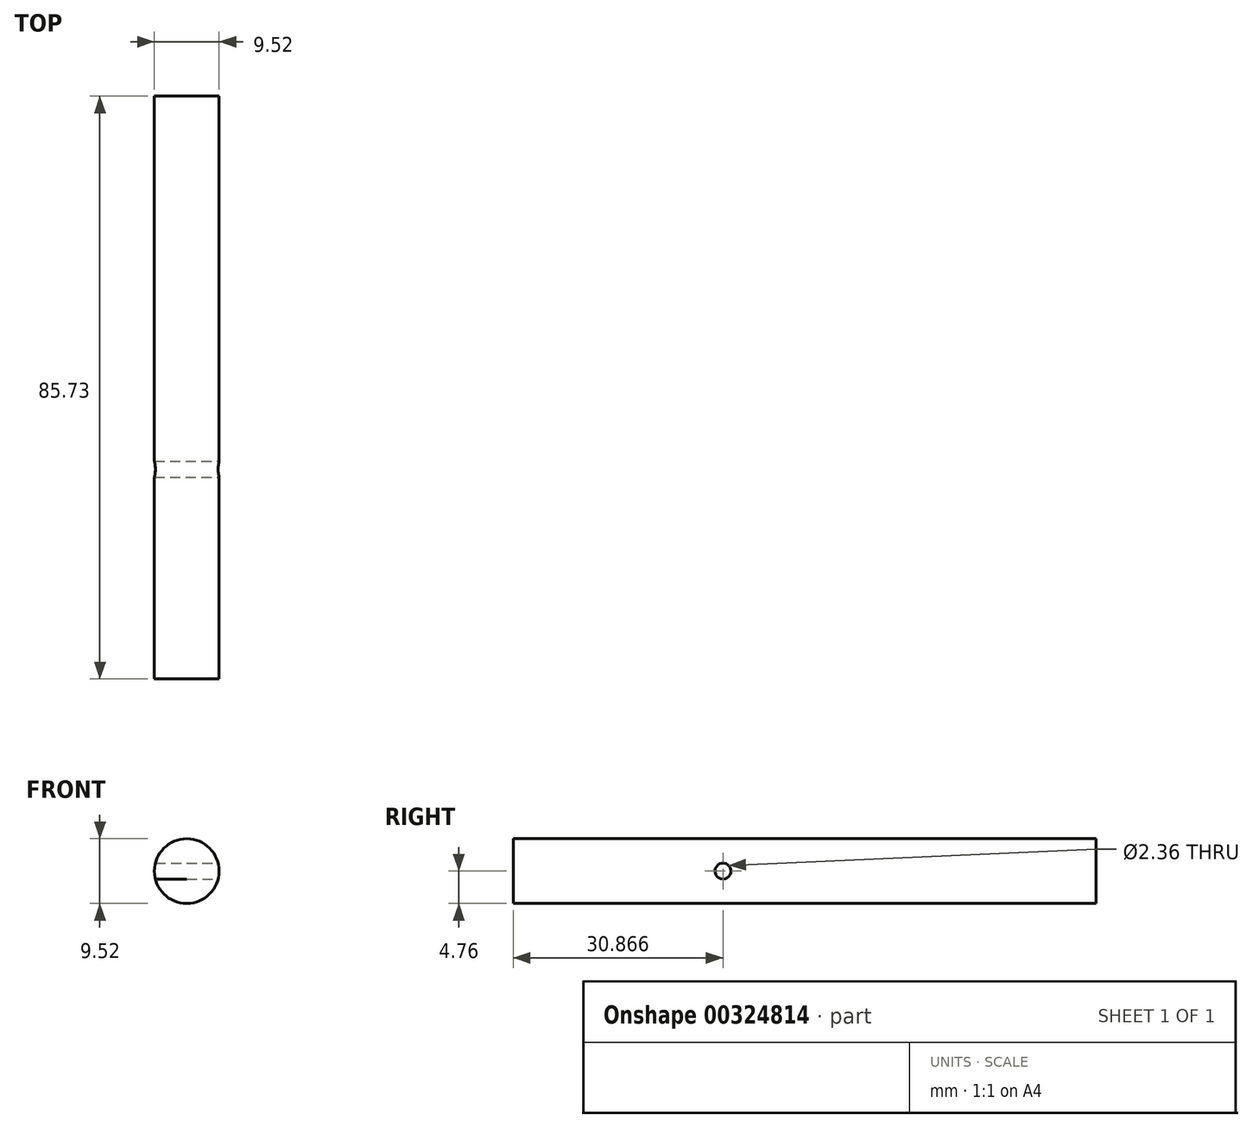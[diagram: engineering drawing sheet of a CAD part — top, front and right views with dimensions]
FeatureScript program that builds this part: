
annotation { "Feature Type Name" : "Feature", "Feature Type Description" : "" }
export const myFeature = defineFeature(function(context is Context, id is Id, definition is map)
    precondition{}
    {
        {
            var Q0;
            Q0=qCreatedBy(makeId("Front.planeOp"),FACE);
            var sketch = newSketch(context, id + "F0", { "sketchPlane" : qUnion([Q0])});
            skCircle(sketch, "E0", {"center": v(0, 0) * mm, "radius": 4.76 * mm});
            skSolve(sketch);
        }
        {
            var Q0;
            Q0=makeQuery(id+"F0.imprint","IMPRINT",FACE,{"disambiguationData":[TD([[makeQuery(id+"F0.imprint","IMPRINT",EDGE,{"derivedFrom":sQuery(id+"F0.wireOp",EDGE,"E0")}),1.0]])]});
            extrude(context, id + "F1", {"entities" : qUnion([Q0]), "depth" : 85.72 * mm, "offsetDistance" : 25.4 * mm});
        }
        {
            var Q0;
            Q0=qCreatedBy(makeId("Right.planeOp"),FACE);
            cPlane(context, id + "F2", {"entities" : qUnion([Q0]), "cplaneType" : CPlaneType.OFFSET, "offset" : 4.78 * mm, "width" : 152.4 * mm, "height" : 152.4 * mm});
        }
        {
            var Q0;
            Q0=qCreatedBy(id+"F2.planeOp",FACE);
            var sketch = newSketch(context, id + "F3", { "sketchPlane" : qUnion([Q0])});
            skCircle(sketch, "E1", {"center": v(-54.86, 0) * mm, "radius": 1.18 * mm});
            skSolve(sketch);
        }
        {
            var Q0;
            Q0=makeQuery(id+"F3.imprint","IMPRINT",FACE,{"disambiguationData":[TD([[makeQuery(id+"F3.imprint","IMPRINT",EDGE,{"derivedFrom":sQuery(id+"F3.wireOp",EDGE,"E1")}),1.0]])]});
            extrude(context, id + "F4", {"entities" : qUnion([Q0]), "operationType" : NewBodyOperationType.REMOVE, "endBound" : BoundingType.THROUGH_ALL, "oppositeDirection" : true, "depth" : 25.4 * mm, "offsetDistance" : 25.4 * mm});
        }
    });
